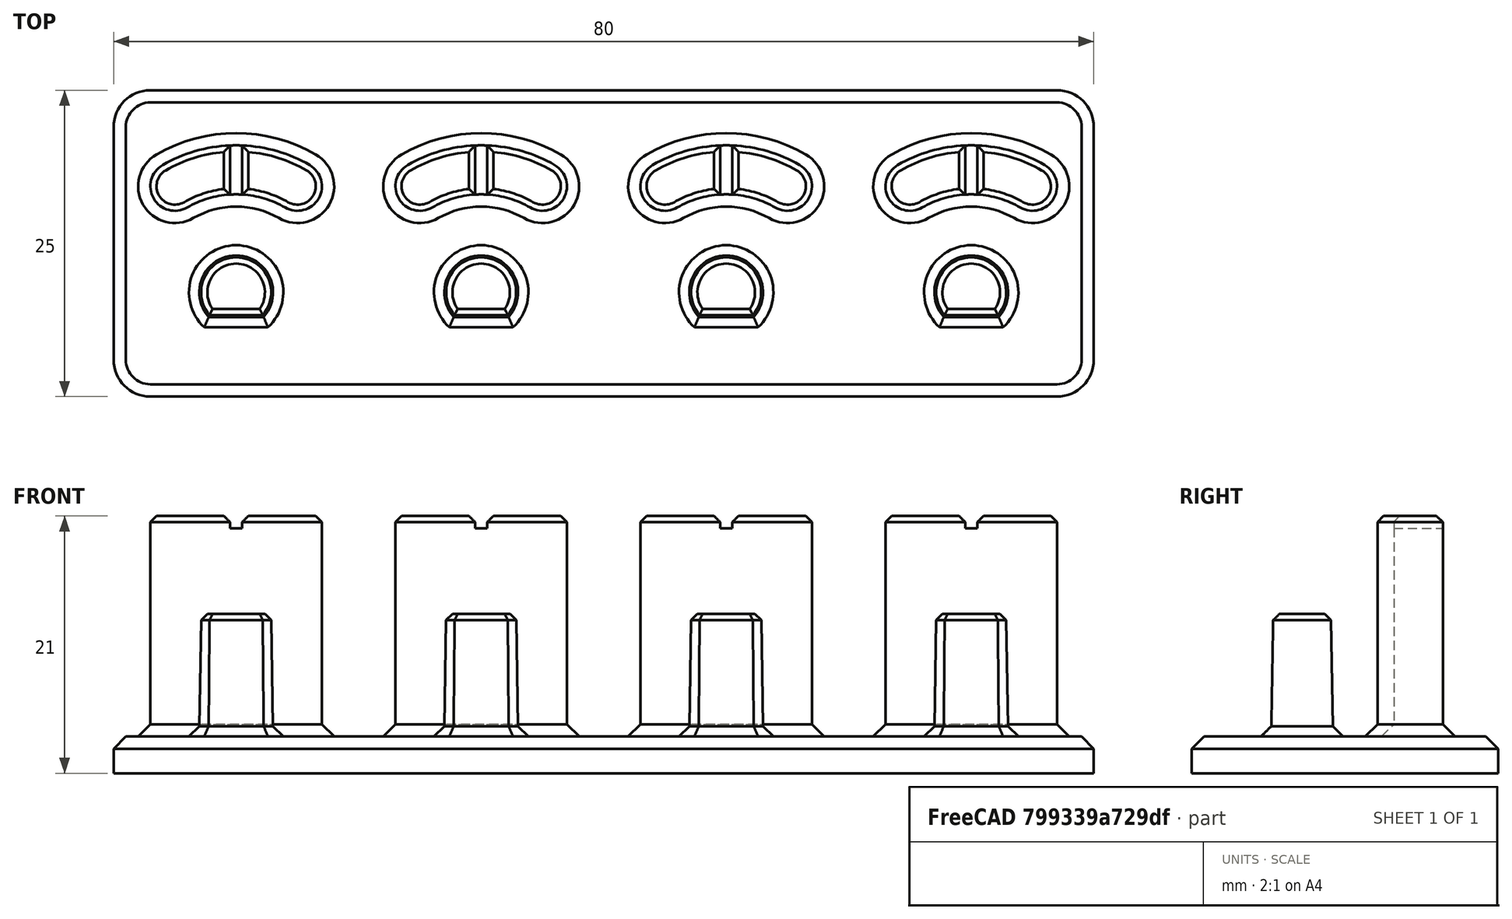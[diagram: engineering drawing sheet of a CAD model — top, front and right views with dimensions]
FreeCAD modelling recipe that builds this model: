
FCSTD DOCUMENT  (FreeCAD 0.20R29177 (Git))
Label: potcap_indicator_alignment_jig
License: All rights reserved
LicenseURL: http://en.wikipedia.org/wiki/All_rights_reserved
objects: Sketcher::SketchObject×4, PartDesign::Pad×2, PartDesign::Pocket×2, PartDesign::Chamfer×2, PartDesign::LinearPattern×1, Mesh::Feature×1, PartDesign::Draft×1, PartDesign::Body×1
note: 20 computed .brp shape members not serialized (recipe doc carries the construction recipe); baked Part::Feature solids carry a one-line shape summary decoded from their .brp

FEATURE [Sketcher::SketchObject] Sketch
  FullyConstrained = true
  MapMode = 5
  Support = -> [XY_Plane]
  sketch-geometry (11):
    g0: LineSegment StartX=-37 StartY=12.5 StartZ=0 EndX=37 EndY=12.5 EndZ=0
    g1: LineSegment StartX=40 StartY=9.5 StartZ=0 EndX=40 EndY=-9.5 EndZ=0
    g2: LineSegment StartX=37 StartY=-12.5 StartZ=0 EndX=-37 EndY=-12.5 EndZ=0
    g3: LineSegment StartX=-40 StartY=-9.5 StartZ=0 EndX=-40 EndY=9.5 EndZ=0
    g4: ArcOfCircle CenterX=-37 CenterY=9.5 CenterZ=0 NormalX=0 NormalY=0 NormalZ=1 AngleXU=0 Radius=3 StartAngle=1.5708 EndAngle=3.14159
    g5: ArcOfCircle CenterX=37 CenterY=9.5 CenterZ=0 NormalX=0 NormalY=0 NormalZ=1 AngleXU=0 Radius=3 StartAngle=8.32e-14 EndAngle=1.5708
    g6: ArcOfCircle CenterX=37 CenterY=-9.5 CenterZ=0 NormalX=0 NormalY=0 NormalZ=1 AngleXU=0 Radius=3 StartAngle=4.71239 EndAngle=6.28319
    g7: ArcOfCircle CenterX=-37 CenterY=-9.5 CenterZ=0 NormalX=0 NormalY=0 NormalZ=1 AngleXU=0 Radius=3 StartAngle=3.14159 EndAngle=4.71239
    g8: LineSegment StartX=-37 StartY=9.5 StartZ=0 EndX=0 EndY=0 EndZ=0
    g9: LineSegment StartX=0 StartY=0 StartZ=0 EndX=37 EndY=9.5 EndZ=0
    g10: LineSegment StartX=-37 StartY=-9.5 StartZ=0 EndX=0 EndY=0 EndZ=0
  constraints (26):
    c: Horizontal(g0)
    c: Horizontal(g2)
    c: Vertical(g1)
    c: Vertical(g3)
    c: Tangent(g0,g4) = 1.5708
    c: Tangent(g3,g4) = 1.5708
    c: Tangent(g0,g5) = 1.5708
    c: Tangent(g1,g5) = 1.5708
    c: Tangent(g1,g6) = 1.5708
    c: Tangent(g2,g6) = 1.5708
    c: Tangent(g2,g7) = 1.5708
    c: Tangent(g3,g7) = 1.5708
    c: Coincident(g8,g4)
    c: Coincident(g8,g9)
    c: Coincident(g9,g5)
    c: Coincident(g10,g7)
    c: Coincident(g10,g8)
    c: Coincident(g8,g-1)
    c: Equal(g10,g8)
    c: Equal(g8,g9)
    c: Equal(g4,g5)
    c: Equal(g5,g6)
    c: Equal(g6,g7)
    c: DistanceX(g3,g1) = 80
    c: DistanceY(g2,g0) = 25
    c: Radius(g4) = 3
FEATURE [PartDesign::Pad] Pad
  Direction = (0,0,1)
  Length = 3
  Length2 = 100
  Profile = -> Sketch
  Type = 0
FEATURE [Sketcher::SketchObject] Sketch001
  AttachmentOffset = pos=(0,0,3) rot=(0,0,1;0rad)
  FullyConstrained = true
  MapMode = 5
  Placement = pos=(0,0,3) rot=(0,0,1;0rad)
  Support = -> [XY_Plane]
  sketch-geometry (7):
    g0: ArcOfCircle CenterX=-30 CenterY=-4 CenterZ=0 NormalX=0 NormalY=0 NormalZ=1 AngleXU=0 Radius=2.85 StartAngle=5.57675 EndAngle=10.1312
    g1: LineSegment StartX=-32.1679 StartY=-5.85 StartZ=0 EndX=-27.8321 EndY=-5.85 EndZ=0
    g2: ArcOfCircle CenterX=-30 CenterY=-4 CenterZ=0 NormalX=0 NormalY=0 NormalZ=1 AngleXU=0 Radius=8 StartAngle=1.0472 EndAngle=2.0944
    g3: ArcOfCircle CenterX=-30 CenterY=-4 CenterZ=0 NormalX=0 NormalY=0 NormalZ=1 AngleXU=0 Radius=12 StartAngle=1.0472 EndAngle=2.0944
    g4: ArcOfCircle CenterX=-25 CenterY=4.66025 CenterZ=0 NormalX=0 NormalY=0 NormalZ=1 AngleXU=0 Radius=2 StartAngle=4.18879 EndAngle=7.33038
    g5: ArcOfCircle CenterX=-35 CenterY=4.66025 CenterZ=0 NormalX=0 NormalY=0 NormalZ=1 AngleXU=0 Radius=2 StartAngle=2.0944 EndAngle=5.23599
    g6: LineSegment StartX=-35 StartY=4.66025 StartZ=0 EndX=-25 EndY=4.66025 EndZ=0
  constraints (19):
    c: Coincident(g1,g0)
    c: Coincident(g1,g0)
    c: Horizontal(g1)
    c: DistanceY(g0,g0) = 1.85
    c: Diameter(g0) = 5.7
    c: DistanceX(g0,g-1) = 30
    c: Coincident(g2,g0)
    c: Coincident(g3,g0)
    c: Tangent(g5,g3) = -1.5708
    c: Tangent(g5,g2) = 1.5708
    c: Tangent(g4,g2) = 1.5708
    c: Tangent(g4,g3) = -1.5708
    c: Coincident(g6,g5)
    c: Coincident(g6,g4)
    c: Horizontal(g6)
    c: DistanceX(g5,g4) = 10
    c: Distance(g5,g0) = 10
    c: Diameter(g5) = 4
    c: DistanceY(g0,g-1) = 4
FEATURE [PartDesign::Pad] Pad001
  BaseFeature = -> Pad
  Direction = (0,0,1)
  Length = 18
  Length2 = 100
  Profile = -> Sketch001
  Type = 0
FEATURE [PartDesign::LinearPattern] LinearPattern
  BaseFeature = -> Pad001
  Direction = -> X_Axis
  Length = 60
  Occurrences = 4
  Originals = -> [Pad001]
FEATURE [Sketcher::SketchObject] Sketch002
  AttachmentOffset = pos=(0,0,13) rot=(0,0,1;0rad)
  FullyConstrained = true
  MapMode = 5
  Placement = pos=(0,0,13) rot=(0,0,1;0rad)
  Support = -> [XY_Plane]
  sketch-geometry (6):
    g0: LineSegment StartX=-42.5 StartY=0 StartZ=0 EndX=42.5 EndY=0 EndZ=0
    g1: LineSegment StartX=42.5 StartY=0 StartZ=0 EndX=42.5 EndY=-15 EndZ=0
    g2: LineSegment StartX=42.5 StartY=-15 StartZ=0 EndX=-42.5 EndY=-15 EndZ=0
    g3: LineSegment StartX=-42.5 StartY=-15 StartZ=0 EndX=-42.5 EndY=0 EndZ=0
    g4: LineSegment StartX=-42.5 StartY=-15 StartZ=0 EndX=0 EndY=0 EndZ=0
    g5: LineSegment StartX=0 StartY=0 StartZ=0 EndX=42.5 EndY=-15 EndZ=0
  constraints (16):
    c: Coincident(g0,g1)
    c: Coincident(g1,g2)
    c: Coincident(g2,g3)
    c: Coincident(g3,g0)
    c: Horizontal(g0)
    c: Horizontal(g2)
    c: Vertical(g1)
    c: Vertical(g3)
    c: PointOnObject(g0,g-1)
    c: Coincident(g2,g4)
    c: Coincident(g4,g-1)
    c: Coincident(g4,g5)
    c: Coincident(g5,g1)
    c: Equal(g4,g5)
    c: DistanceY(g3,g3) = 15
    c: DistanceX(g2,g2) = 85
FEATURE [PartDesign::Pocket] Pocket
  BaseFeature = -> LinearPattern
  Direction = (0,0,-1)
  Length = 5
  Length2 = 100
  Profile = -> Sketch002
  Reversed = true
  Type = 1
FEATURE [Sketcher::SketchObject] Sketch003
  AttachmentOffset = pos=(0,0,20) rot=(0,0,1;0rad)
  FullyConstrained = true
  MapMode = 5
  Placement = pos=(0,0,20) rot=(0,0,1;0rad)
  Support = -> [XY_Plane]
  sketch-geometry (30):
    g0: LineSegment StartX=-30.5 StartY=12 StartZ=0 EndX=-29.5 EndY=12 EndZ=0
    g1: LineSegment StartX=-29.5 StartY=12 StartZ=0 EndX=-29.5 EndY=2 EndZ=0
    g2: LineSegment StartX=-29.5 StartY=2 StartZ=0 EndX=-30.5 EndY=2 EndZ=0
    g3: LineSegment StartX=-30.5 StartY=2 StartZ=0 EndX=-30.5 EndY=12 EndZ=0
    g4: LineSegment StartX=-10.5 StartY=12 StartZ=0 EndX=-9.5 EndY=12 EndZ=0
    g5: LineSegment StartX=-9.5 StartY=12 StartZ=0 EndX=-9.5 EndY=2 EndZ=0
    g6: LineSegment StartX=-9.5 StartY=2 StartZ=0 EndX=-10.5 EndY=2 EndZ=0
    g7: LineSegment StartX=-10.5 StartY=2 StartZ=0 EndX=-10.5 EndY=12 EndZ=0
    g8: LineSegment StartX=9.5 StartY=12 StartZ=0 EndX=10.5 EndY=12 EndZ=0
    g9: LineSegment StartX=10.5 StartY=12 StartZ=0 EndX=10.5 EndY=2 EndZ=0
    g10: LineSegment StartX=10.5 StartY=2 StartZ=0 EndX=9.5 EndY=2 EndZ=0
    g11: LineSegment StartX=9.5 StartY=2 StartZ=0 EndX=9.5 EndY=12 EndZ=0
    g12: LineSegment StartX=29.5 StartY=12 StartZ=0 EndX=30.5 EndY=12 EndZ=0
    g13: LineSegment StartX=30.5 StartY=12 StartZ=0 EndX=30.5 EndY=2 EndZ=0
    g14: LineSegment StartX=30.5 StartY=2 StartZ=0 EndX=29.5 EndY=2 EndZ=0
    g15: LineSegment StartX=29.5 StartY=2 StartZ=0 EndX=29.5 EndY=12 EndZ=0
    g16: LineSegment StartX=-30.5 StartY=2 StartZ=0 EndX=-30 EndY=0 EndZ=0
    g17: LineSegment StartX=-30 StartY=0 StartZ=0 EndX=-29.5 EndY=2 EndZ=0
    g18: LineSegment StartX=-10.5 StartY=2 StartZ=0 EndX=-10 EndY=0 EndZ=0
    g19: LineSegment StartX=-10 StartY=0 StartZ=0 EndX=-9.5 EndY=2 EndZ=0
    g20: LineSegment StartX=9.5 StartY=2 StartZ=0 EndX=10 EndY=0 EndZ=0
    g21: LineSegment StartX=10 StartY=0 StartZ=0 EndX=10.5 EndY=2 EndZ=0
    g22: LineSegment StartX=29.5 StartY=2 StartZ=0 EndX=30 EndY=0 EndZ=0
    g23: LineSegment StartX=30 StartY=0 StartZ=0 EndX=30.5 EndY=2 EndZ=0
    g24: LineSegment StartX=-30 StartY=0 StartZ=0 EndX=-20 EndY=0 EndZ=0
    g25: LineSegment StartX=-20 StartY=0 StartZ=0 EndX=-10 EndY=0 EndZ=0
    g26: LineSegment StartX=-10 StartY=0 StartZ=0 EndX=0 EndY=0 EndZ=0
    g27: LineSegment StartX=0 StartY=0 StartZ=0 EndX=10 EndY=0 EndZ=0
    g28: LineSegment StartX=10 StartY=0 StartZ=0 EndX=20 EndY=0 EndZ=0
    g29: LineSegment StartX=20 StartY=0 StartZ=0 EndX=30 EndY=0 EndZ=0
  constraints (82):
    c: Coincident(g0,g1)
    c: Coincident(g1,g2)
    c: Coincident(g2,g3)
    c: Coincident(g3,g0)
    c: Horizontal(g0)
    c: Horizontal(g2)
    c: Vertical(g1)
    c: Vertical(g3)
    c: Coincident(g4,g5)
    c: Coincident(g5,g6)
    c: Coincident(g6,g7)
    c: Coincident(g7,g4)
    c: Horizontal(g4)
    c: Horizontal(g6)
    c: Vertical(g5)
    c: Vertical(g7)
    c: Coincident(g8,g9)
    c: Coincident(g9,g10)
    c: Coincident(g10,g11)
    c: Coincident(g11,g8)
    c: Horizontal(g8)
    c: Horizontal(g10)
    c: Vertical(g9)
    c: Vertical(g11)
    c: Coincident(g12,g13)
    c: Coincident(g13,g14)
    c: Coincident(g14,g15)
    c: Coincident(g15,g12)
    c: Horizontal(g12)
    c: Horizontal(g14)
    c: Vertical(g13)
    c: Vertical(g15)
    c: Equal(g15,g11)
    c: Equal(g11,g7)
    c: Equal(g7,g3)
    c: Equal(g0,g4)
    c: Equal(g4,g8)
    c: Equal(g8,g12)
    c: Coincident(g2,g16)
    c: PointOnObject(g16,g-1)
    c: Coincident(g16,g17)
    c: Coincident(g17,g1)
    c: Coincident(g6,g18)
    c: PointOnObject(g18,g-1)
    c: Coincident(g18,g19)
    c: Coincident(g19,g5)
    c: Coincident(g10,g20)
    c: PointOnObject(g20,g-1)
    c: Coincident(g20,g21)
    c: Coincident(g21,g9)
    c: Coincident(g14,g22)
    c: PointOnObject(g22,g-1)
    c: Coincident(g22,g23)
    c: Coincident(g23,g13)
    c: Equal(g23,g22)
    c: Equal(g22,g21)
    c: Equal(g21,g20)
    c: Equal(g20,g19)
    c: Equal(g19,g18)
    c: Equal(g18,g17)
    c: Equal(g17,g16)
    c: Coincident(g16,g24)
    c: Coincident(g24,g25)
    c: Coincident(g25,g18)
    c: Coincident(g25,g26)
    c: Coincident(g26,g27)
    c: Coincident(g27,g20)
    c: Coincident(g27,g28)
    c: Coincident(g28,g29)
    c: Coincident(g29,g22)
    c: Coincident(g26,g-1)
    c: PointOnObject(g24,g-1)
    c: PointOnObject(g28,g-1)
    c: Equal(g29,g28)
    c: Equal(g28,g27)
    c: Equal(g27,g26)
    c: Equal(g26,g25)
    c: Equal(g25,g24)
    c: DistanceX(g16,g22) = 60
    c: DistanceX(g0,g0) = 1
    c: DistanceY(g3,g3) = 10
    c: DistanceY(g16,g16) = 2
FEATURE [PartDesign::Pocket] Pocket001
  BaseFeature = -> Pocket
  Direction = (0,0,-1)
  Length = 5
  Length2 = 100
  Profile = -> Sketch003
  Reversed = true
  Type = 1
FEATURE [PartDesign::Chamfer] Chamfer
  Angle = 45
  Base = -> Pocket001 [Face38,Face54,Face39,Face37,Face49,Face44,Face36,Face44,Face49,Face35,Face39,Face54,Face40,Face45,Face50,Face55]
  BaseFeature = -> Pocket001
  ChamferType = 0
  FlipDirection = false
  Size = 0.5
  Size2 = 1
  SupportTransform = false
  UseAllEdges = false
FEATURE [PartDesign::Chamfer] Chamfer001
  Angle = 45
  Base = -> Chamfer [Face4]
  BaseFeature = -> Chamfer
  ChamferType = 0
  FlipDirection = false
  Size = 1
  Size2 = 1
  SupportTransform = false
  UseAllEdges = false
FEATURE [Mesh::Feature] potcap_indicator_alignment_jig_Body  label="old"
FEATURE [PartDesign::Draft] Draft
  Angle = 1
  Base = -> Chamfer001 [Face2,Face1,Face48,Face47,Face50,Face49,Face52,Face51]
  BaseFeature = -> Chamfer001
  NeutralPlane = -> Chamfer001 [Face113]
  SupportTransform = false
FEATURE [PartDesign::Body] Body
  Group = -> [Sketch,Pad,Sketch001,Pad001,LinearPattern,Sketch002,Pocket,Sketch003,Pocket001,Chamfer,Chamfer001,Draft]
  Origin = -> Origin
  Tip = -> Draft
